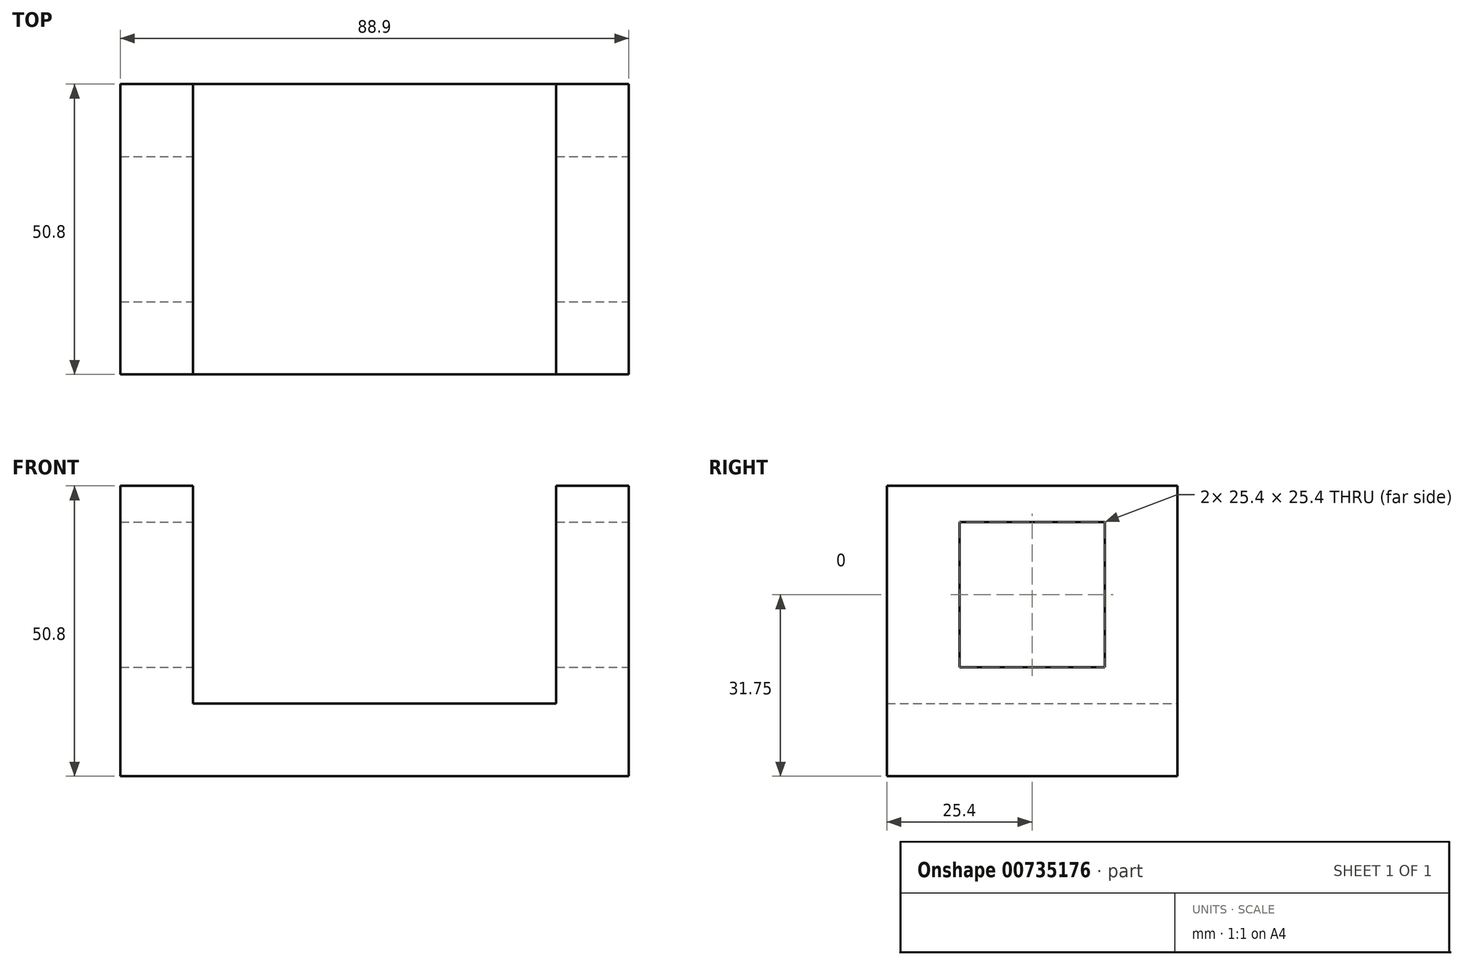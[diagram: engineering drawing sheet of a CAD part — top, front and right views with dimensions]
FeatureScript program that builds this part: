
annotation { "Feature Type Name" : "Feature", "Feature Type Description" : "" }
export const myFeature = defineFeature(function(context is Context, id is Id, definition is map)
    precondition{}
    {
        {
            var Q0;
            Q0=qCreatedBy(makeId("Front.planeOp"),FACE);
            var sketch = newSketch(context, id + "F0", { "sketchPlane" : qUnion([Q0])});
            skLineSegment(sketch, "E0", {"start": v(-51.75, 38.1) * mm, "end": v(-51.75, -12.7) * mm});
            skLineSegment(sketch, "E1", {"start": v(-51.75, -12.7) * mm, "end": v(37.15, -12.7) * mm});
            skLineSegment(sketch, "E2", {"start": v(37.15, -12.7) * mm, "end": v(37.15, 38.1) * mm});
            skLineSegment(sketch, "E3", {"start": v(37.15, 38.1) * mm, "end": v(24.45, 38.1) * mm});
            skLineSegment(sketch, "E4", {"start": v(24.45, 38.1) * mm, "end": v(24.45, 0) * mm});
            skLineSegment(sketch, "E5", {"start": v(-51.75, 38.1) * mm, "end": v(-39.05, 38.1) * mm});
            skLineSegment(sketch, "E6", {"start": v(-39.05, 38.1) * mm, "end": v(-39.05, 0) * mm});
            skLineSegment(sketch, "E7", {"start": v(-39.05, 0) * mm, "end": v(24.45, 0) * mm});
            skSolve(sketch);
        }
        {
            var Q0;
            Q0=makeQuery(id+"F0.imprint","IMPRINT",FACE,{"disambiguationData":[TD([[makeQuery(id+"F0.imprint","IMPRINT",EDGE,{"derivedFrom":sQuery(id+"F0.wireOp",EDGE,"E0")}),1.0]])]});
            extrude(context, id + "F1", {"entities" : qUnion([Q0]), "depth" : 50.8 * mm, "offsetDistance" : 25.4 * mm});
        }
        {
            var Q0;
            Q0=makeQuery(id+"F1.opExtrude","SWEPT_FACE",FACE,{"disambiguationData":[OSD([sQuery(id+"F0.wireOp",EDGE,"E2")])]});
            var sketch = newSketch(context, id + "F2", { "sketchPlane" : qUnion([Q0])});
            skLineSegment(sketch, "E8.bottom", {"start": v(-38.1, 31.75) * mm, "end": v(-12.7, 31.75) * mm});
            skLineSegment(sketch, "E8.top", {"start": v(-38.1, 6.35) * mm, "end": v(-12.7, 6.35) * mm});
            skLineSegment(sketch, "E8.left", {"start": v(-38.1, 31.75) * mm, "end": v(-38.1, 6.35) * mm});
            skLineSegment(sketch, "E8.right", {"start": v(-12.7, 31.75) * mm, "end": v(-12.7, 6.35) * mm});
            skSolve(sketch);
        }
        {
            var Q0;
            Q0 = qSketchRegion(id + "F2", true);
            extrude(context, id + "F3", {"entities" : qUnion([Q0]), "operationType" : NewBodyOperationType.REMOVE, "endBound" : BoundingType.THROUGH_ALL, "oppositeDirection" : true, "depth" : 25.4 * mm, "offsetDistance" : 25.4 * mm});
        }
    });
